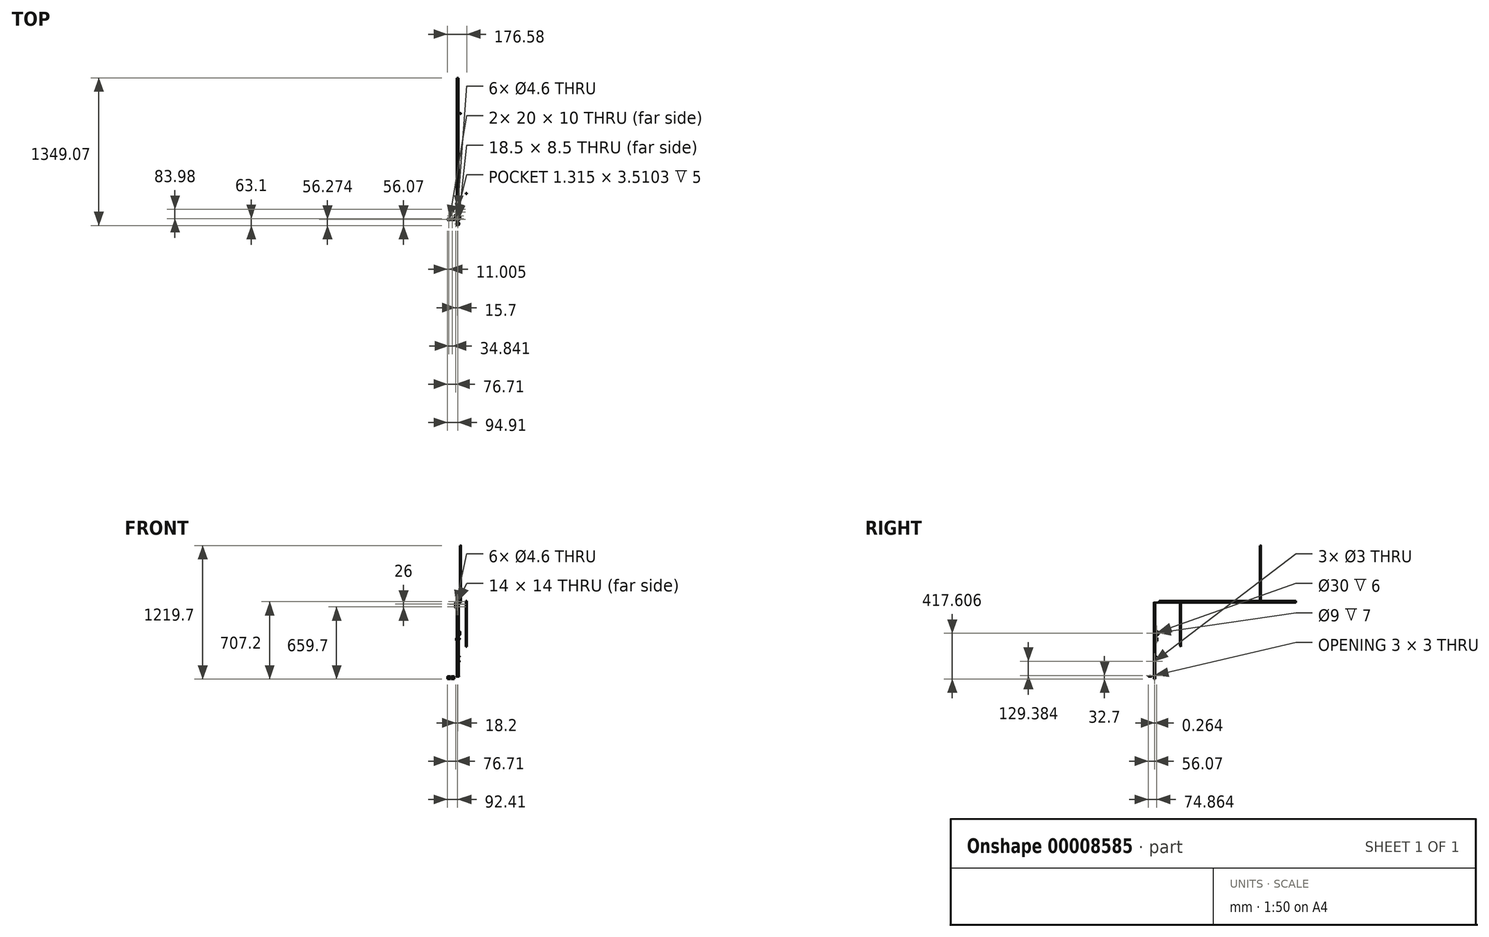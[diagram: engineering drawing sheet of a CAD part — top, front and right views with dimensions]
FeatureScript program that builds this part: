
annotation { "Feature Type Name" : "Feature", "Feature Type Description" : "" }
export const myFeature = defineFeature(function(context is Context, id is Id, definition is map)
    precondition{}
    {
        {
            var Q0;
            Q0=qCreatedBy(makeId("Front.planeOp"),FACE);
            var sketch = newSketch(context, id + "F0", { "sketchPlane" : qUnion([Q0])});
            skLineSegment(sketch, "E0.rect.bottom", {"start": v(-7.5, 7.5) * mm, "end": v(7.5, 7.5) * mm});
            skLineSegment(sketch, "E0.rect.top", {"start": v(-7.5, -7.5) * mm, "end": v(7.5, -7.5) * mm});
            skLineSegment(sketch, "E0.rect.left", {"start": v(-7.5, 7.5) * mm, "end": v(-7.5, -7.5) * mm});
            skLineSegment(sketch, "E0.rect.right", {"start": v(7.5, 7.5) * mm, "end": v(7.5, -7.5) * mm});
            skPoint(sketch, "E0.rect.middle", {"position": v(0, 0) * mm});
            skLineSegment(sketch, "E1.rect.bottom", {"start": v(-7, 7) * mm, "end": v(7, 7) * mm});
            skLineSegment(sketch, "E1.rect.top", {"start": v(-7, -7) * mm, "end": v(7, -7) * mm});
            skLineSegment(sketch, "E1.rect.left", {"start": v(-7, 7) * mm, "end": v(-7, -7) * mm});
            skLineSegment(sketch, "E1.rect.right", {"start": v(7, 7) * mm, "end": v(7, -7) * mm});
            skSolve(sketch);
        }
        {
            var Q0;
            Q0=qSketchRegion(id+"F0",true);
            extrude(context, id + "F1", {"entities" : qUnion([Q0]), "depth" : 950 * mm});
        }
        {
            var Q0;
            Q0=makeQuery(id+"F1.opExtrude","SWEPT_FACE",FACE,{"disambiguationData":[OSD([sQuery(id+"F0.wireOp",EDGE,"E0.rect.left")])]});
            var sketch = newSketch(context, id + "F2", { "sketchPlane" : qUnion([Q0])});
            skLineSegment(sketch, "E2.bottom", {"start": v(998.04, -7.5) * mm, "end": v(950, -7.5) * mm});
            skLineSegment(sketch, "E2.top", {"start": v(998, -9.5) * mm, "end": v(950, -9.5) * mm});
            skLineSegment(sketch, "E2.right", {"start": v(950, -7.5) * mm, "end": v(950, -9.5) * mm});
            skLineSegment(sketch, "E3.top", {"start": v(1000, -57.5) * mm, "end": v(998, -57.5) * mm});
            skLineSegment(sketch, "E3.left", {"start": v(1000, -9.5) * mm, "end": v(1000, -57.5) * mm});
            skLineSegment(sketch, "E3.right", {"start": v(998, -9.5) * mm, "end": v(998, -57.5) * mm});
            skArc(sketch, "E4", {"start": v(1000, -9.5) * mm, "mid": v(999.4, -8.07) * mm, "end": v(997.96, -7.5) * mm});
            skSolve(sketch);
        }
        {
            var Q0;
            Q0=qSketchRegion(id+"F2",true);
            extrude(context, id + "F3", {"entities" : qUnion([Q0]), "depth" : 16.4 * mm});
        }
        {
            var Q0;
            Q0=makeQuery(id+"F3.opExtrude","SWEPT_FACE",FACE,{"disambiguationData":[OSD([sQuery(id+"F2.wireOp",EDGE,"E3.left")])]});
            var sketch = newSketch(context, id + "F4", { "sketchPlane" : qUnion([Q0])});
            skCircle(sketch, "E5", {"center": v(-15.7, -21.5) * mm, "radius": 2.3 * mm});
            skCircle(sketch, "E6", {"center": v(-15.7, -45.5) * mm, "radius": 2.3 * mm});
            skSolve(sketch);
        }
        {
            var Q0;
            Q0=qSketchRegion(id+"F4",true);
            extrude(context, id + "F5", {"entities" : qUnion([Q0]), "operationType" : NewBodyOperationType.REMOVE, "oppositeDirection" : true, "depth" : 25 * mm});
        }
        {
            var Q0;
            Q0=makeQuery(id+"F3.opExtrude","SWEPT_FACE",FACE,{"disambiguationData":[OSD([sQuery(id+"F2.wireOp",EDGE,"E2.bottom")])]});
            var sketch = newSketch(context, id + "F6", { "sketchPlane" : qUnion([Q0])});
            skCircle(sketch, "E7", {"center": v(0, 12) * mm, "radius": 2.3 * mm});
            skCircle(sketch, "E8", {"center": v(0, -12) * mm, "radius": 2.3 * mm});
            skCircle(sketch, "E9", {"center": v(-15.7, -985.97) * mm, "radius": 2.3 * mm});
            skCircle(sketch, "E10", {"center": v(-15.7, -961.99) * mm, "radius": 2.3 * mm});
            skSolve(sketch);
        }
        {
            var Q0;
            Q0=makeQuery(id+"F6.imprint","IMPRINT",FACE,{"disambiguationData":[TD([[makeQuery(id+"F6.imprint","IMPRINT",EDGE,{"derivedFrom":sQuery(id+"F6.wireOp",EDGE,"E9")}),1.0]])]});
            var Q1;
            Q1=makeQuery(id+"F6.imprint","IMPRINT",FACE,{"disambiguationData":[TD([[makeQuery(id+"F6.imprint","IMPRINT",EDGE,{"derivedFrom":sQuery(id+"F6.wireOp",EDGE,"E10")}),1.0]])]});
            extrude(context, id + "F7", {"entities" : qUnion([Q0, Q1]), "operationType" : NewBodyOperationType.REMOVE, "oppositeDirection" : true, "depth" : 3 * mm});
        }
        {
            var Q0;
            Q0=makeQuery(id+"F3.opExtrude","SWEPT_FACE",FACE,{"disambiguationData":[OSD([sQuery(id+"F2.wireOp",EDGE,"E2.top")])]});
            var sketch = newSketch(context, id + "F8", { "sketchPlane" : qUnion([Q0])});
            skLineSegment(sketch, "E11.bottom", {"start": v(-7.5, 998) * mm, "end": v(12.5, 998) * mm});
            skLineSegment(sketch, "E11.top", {"start": v(-7.5, 988) * mm, "end": v(12.5, 988) * mm});
            skLineSegment(sketch, "E11.left", {"start": v(-7.5, 998) * mm, "end": v(-7.5, 988) * mm});
            skLineSegment(sketch, "E11.right", {"start": v(12.5, 998) * mm, "end": v(12.5, 988) * mm});
            skLineSegment(sketch, "E12.rect.bottom", {"start": v(-6.75, 988.75) * mm, "end": v(11.75, 988.75) * mm});
            skLineSegment(sketch, "E12.rect.top", {"start": v(-6.75, 997.25) * mm, "end": v(11.75, 997.25) * mm});
            skLineSegment(sketch, "E12.rect.left", {"start": v(-6.75, 988.75) * mm, "end": v(-6.75, 997.25) * mm});
            skLineSegment(sketch, "E12.rect.right", {"start": v(11.75, 988.75) * mm, "end": v(11.75, 997.25) * mm});
            skPoint(sketch, "E12.rect.middle", {"position": v(2.5, 993) * mm});
            skSolve(sketch);
        }
        {
            var Q0;
            Q0=makeQuery(id+"F8.imprint","IMPRINT",FACE,{"disambiguationData":[TD([[makeQuery(id+"F8.imprint","IMPRINT",EDGE,{"derivedFrom":sQuery(id+"F8.wireOp",EDGE,"E11.bottom")}),-1.0]])]});
            extrude(context, id + "F9", {"entities" : qUnion([Q0]), "depth" : 673 * mm});
        }
        {
            var Q0;
            Q0=makeQuery(id+"F9.opExtrude","SWEPT_FACE",FACE,{"disambiguationData":[OSD([sQuery(id+"F8.wireOp",EDGE,"E11.bottom")])]});
            var sketch = newSketch(context, id + "F10", { "sketchPlane" : qUnion([Q0])});
            skCircle(sketch, "E13", {"center": v(2.5, -23.5) * mm, "radius": 2.3 * mm});
            skCircle(sketch, "E14", {"center": v(2.5, -47.5) * mm, "radius": 2.3 * mm});
            skSolve(sketch);
        }
        {
            var Q0;
            Q0=qSketchRegion(id+"F10",true);
            extrude(context, id + "F11", {"entities" : qUnion([Q0]), "operationType" : NewBodyOperationType.REMOVE, "oppositeDirection" : true, "depth" : 11 * mm});
        }
        {
            var Q0;
            Q0=makeQuery(id+"F1.opExtrude","SWEPT_FACE",FACE,{"disambiguationData":[OSD([sQuery(id+"F0.wireOp",EDGE,"E0.rect.top")])]});
            var sketch = newSketch(context, id + "F12", { "sketchPlane" : qUnion([Q0])});
            skCircle(sketch, "E15", {"center": v(0, 901.99) * mm, "radius": 2.3 * mm});
            skCircle(sketch, "E16", {"center": v(0, 925.97) * mm, "radius": 2.3 * mm});
            skLineSegment(sketch, "E17", {"start": v(0, 950) * mm, "end": v(0, 925.97) * mm});
            skLineSegment(sketch, "E18", {"start": v(0, 925.97) * mm, "end": v(0, 901.99) * mm});
            skSolve(sketch);
        }
        {
            var Q0;
            Q0=makeQuery(id+"F12.imprint","IMPRINT",FACE,{"disambiguationData":[TD([[makeQuery(id+"F12.imprint","IMPRINT",EDGE,{"derivedFrom":sQuery(id+"F12.wireOp",EDGE,"E15")}),1.0]])]});
            var Q1;
            Q1=makeQuery(id+"F12.imprint","IMPRINT",FACE,{"disambiguationData":[TD([[makeQuery(id+"F12.imprint","IMPRINT",EDGE,{"derivedFrom":sQuery(id+"F12.wireOp",EDGE,"E16")}),1.0]])]});
            extrude(context, id + "F13", {"entities" : qUnion([Q0, Q1]), "operationType" : NewBodyOperationType.REMOVE, "oppositeDirection" : true, "depth" : 25 * mm});
        }
        {
            var Q0;
            Q0=makeQuery(id+"F9.opExtrude","CAP_FACE",FACE,{"disambiguationData":[OSD([sQuery(id+"F8.wireOp",EDGE,"E11.bottom"),sQuery(id+"F8.wireOp",EDGE,"E11.top"),sQuery(id+"F8.wireOp",EDGE,"E11.left"),sQuery(id+"F8.wireOp",EDGE,"E11.right"),sQuery(id+"F8.wireOp",EDGE,"E12.rect.bottom"),sQuery(id+"F8.wireOp",EDGE,"E12.rect.top"),sQuery(id+"F8.wireOp",EDGE,"E12.rect.left"),sQuery(id+"F8.wireOp",EDGE,"E12.rect.right")])],"isStart":false});
            var sketch = newSketch(context, id + "F14", { "sketchPlane" : qUnion([Q0])});
            skCircle(sketch, "E19", {"center": v(1.66, 1034.07) * mm, "radius": 15 * mm});
            skSolve(sketch);
        }
        {
            var Q0;
            Q0=qSketchRegion(id+"F14",true);
            extrude(context, id + "F15", {"entities" : qUnion([Q0]), "depth" : 2 * mm});
        }
        {
            var Q0;
            Q0=makeQuery(id+"F15.opExtrude","CAP_FACE",FACE,{"disambiguationData":[OSD([sQuery(id+"F14.wireOp",EDGE,"E19")])],"isStart":true});
            var sketch = newSketch(context, id + "F16", { "sketchPlane" : qUnion([Q0])});
            skLineSegment(sketch, "E20.rect.bottom", {"start": v(-7.59, -1038.32) * mm, "end": v(10.91, -1038.32) * mm});
            skLineSegment(sketch, "E20.rect.top", {"start": v(-7.59, -1029.82) * mm, "end": v(10.91, -1029.82) * mm});
            skLineSegment(sketch, "E20.rect.left", {"start": v(-7.59, -1038.32) * mm, "end": v(-7.59, -1029.82) * mm});
            skLineSegment(sketch, "E20.rect.right", {"start": v(10.91, -1038.32) * mm, "end": v(10.91, -1029.82) * mm});
            skPoint(sketch, "E20.rect.middle", {"position": v(1.66, -1034.07) * mm});
            skSolve(sketch);
        }
        {
            var Q0;
            Q0=qSketchRegion(id+"F16",true);
            extrude(context, id + "F17", {"entities" : qUnion([Q0]), "operationType" : NewBodyOperationType.ADD, "depth" : 3 * mm});
        }
        {
            var Q0;
            Q0=makeQuery(id+"F9.opExtrude","CAP_FACE",FACE,{"disambiguationData":[OSD([sQuery(id+"F8.wireOp",EDGE,"E11.bottom"),sQuery(id+"F8.wireOp",EDGE,"E11.top"),sQuery(id+"F8.wireOp",EDGE,"E11.left"),sQuery(id+"F8.wireOp",EDGE,"E11.right"),sQuery(id+"F8.wireOp",EDGE,"E12.rect.bottom"),sQuery(id+"F8.wireOp",EDGE,"E12.rect.top"),sQuery(id+"F8.wireOp",EDGE,"E12.rect.left"),sQuery(id+"F8.wireOp",EDGE,"E12.rect.right")])],"isStart":false});
            var sketch = newSketch(context, id + "F18", { "sketchPlane" : qUnion([Q0])});
            skLineSegment(sketch, "E21.rect.bottom", {"start": v(-56.56, 987.8) * mm, "end": v(-36.56, 987.8) * mm});
            skLineSegment(sketch, "E21.rect.top", {"start": v(-56.56, 997.8) * mm, "end": v(-36.56, 997.8) * mm});
            skLineSegment(sketch, "E21.rect.left", {"start": v(-56.56, 987.8) * mm, "end": v(-56.56, 997.8) * mm});
            skLineSegment(sketch, "E21.rect.right", {"start": v(-36.56, 987.8) * mm, "end": v(-36.56, 997.8) * mm});
            skPoint(sketch, "E21.rect.middle", {"position": v(-46.56, 992.8) * mm});
            skLineSegment(sketch, "E22.rect.bottom", {"start": v(-91.4, 987.8) * mm, "end": v(-71.4, 987.8) * mm});
            skLineSegment(sketch, "E22.rect.top", {"start": v(-91.4, 997.8) * mm, "end": v(-71.4, 997.8) * mm});
            skLineSegment(sketch, "E22.rect.left", {"start": v(-91.4, 987.8) * mm, "end": v(-91.4, 997.8) * mm});
            skLineSegment(sketch, "E22.rect.right", {"start": v(-71.4, 987.8) * mm, "end": v(-71.4, 997.8) * mm});
            skPoint(sketch, "E22.rect.middle", {"position": v(-81.4, 992.8) * mm});
            skLineSegment(sketch, "E23.rect.bottom", {"start": v(-92.4, 986.8) * mm, "end": v(-70.4, 986.8) * mm});
            skLineSegment(sketch, "E23.rect.top", {"start": v(-92.4, 998.8) * mm, "end": v(-70.4, 998.8) * mm});
            skLineSegment(sketch, "E23.rect.left", {"start": v(-92.4, 986.8) * mm, "end": v(-92.4, 998.8) * mm});
            skLineSegment(sketch, "E23.rect.right", {"start": v(-70.4, 986.8) * mm, "end": v(-70.4, 998.8) * mm});
            skLineSegment(sketch, "E24.rect.bottom", {"start": v(-57.56, 986.8) * mm, "end": v(-35.56, 986.8) * mm});
            skLineSegment(sketch, "E24.rect.top", {"start": v(-57.56, 998.8) * mm, "end": v(-35.56, 998.8) * mm});
            skLineSegment(sketch, "E24.rect.left", {"start": v(-57.56, 986.8) * mm, "end": v(-57.56, 998.8) * mm});
            skLineSegment(sketch, "E24.rect.right", {"start": v(-35.56, 986.8) * mm, "end": v(-35.56, 998.8) * mm});
            skSolve(sketch);
        }
        {
            var Q0;
            Q0=qSketchRegion(id+"F18",true);
            extrude(context, id + "F19", {"entities" : qUnion([Q0]), "depth" : 24.7 * mm});
        }
        {
            var Q0;
            Q0=makeQuery(id+"F19.opExtrude","SWEPT_FACE",FACE,{"disambiguationData":[OSD([sQuery(id+"F18.wireOp",EDGE,"E23.rect.bottom")])]});
            var sketch = newSketch(context, id + "F20", { "sketchPlane" : qUnion([Q0])});
            skLineSegment(sketch, "E25", {"start": v(81.4, -528.03) * mm, "end": v(87.58, -521.85) * mm});
            skLineSegment(sketch, "E26", {"start": v(87.58, -521.85) * mm, "end": v(81.4, -515.68) * mm});
            skLineSegment(sketch, "E27", {"start": v(81.4, -515.68) * mm, "end": v(75.23, -521.85) * mm});
            skLineSegment(sketch, "E28", {"start": v(75.23, -521.85) * mm, "end": v(81.4, -528.03) * mm});
            skSolve(sketch);
        }
        {
            var Q0;
            Q0=qSketchRegion(id+"F20",true);
            extrude(context, id + "F21", {"entities" : qUnion([Q0]), "operationType" : NewBodyOperationType.REMOVE, "oppositeDirection" : true, "depth" : 25 * mm});
        }
        {
            var Q0;
            Q0=makeQuery(id+"F19.opExtrude","CAP_FACE",FACE,{"disambiguationData":[OSD([sQuery(id+"F18.wireOp",EDGE,"E22.rect.bottom"),sQuery(id+"F18.wireOp",EDGE,"E22.rect.top"),sQuery(id+"F18.wireOp",EDGE,"E22.rect.left"),sQuery(id+"F18.wireOp",EDGE,"E22.rect.right"),sQuery(id+"F18.wireOp",EDGE,"E23.rect.bottom"),sQuery(id+"F18.wireOp",EDGE,"E23.rect.top"),sQuery(id+"F18.wireOp",EDGE,"E23.rect.left"),sQuery(id+"F18.wireOp",EDGE,"E23.rect.right")])],"isStart":false});
            var sketch = newSketch(context, id + "F22", { "sketchPlane" : qUnion([Q0])});
            skLineSegment(sketch, "E29", {"start": v(-70.4, 998.8) * mm, "end": v(-63.9, 998.8) * mm});
            skLineSegment(sketch, "E30", {"start": v(-63.9, 998.8) * mm, "end": v(-63.9, 997.8) * mm});
            skLineSegment(sketch, "E31", {"start": v(-63.9, 997.8) * mm, "end": v(-70.4, 997.8) * mm});
            skLineSegment(sketch, "E32", {"start": v(-70.4, 986.8) * mm, "end": v(-63.9, 986.8) * mm});
            skLineSegment(sketch, "E33", {"start": v(-63.9, 986.8) * mm, "end": v(-63.9, 987.8) * mm});
            skLineSegment(sketch, "E34", {"start": v(-63.9, 987.8) * mm, "end": v(-70.4, 987.8) * mm});
            skLineSegment(sketch, "E35", {"start": v(-35.56, 998.8) * mm, "end": v(-29.06, 998.8) * mm});
            skLineSegment(sketch, "E36", {"start": v(-29.06, 998.8) * mm, "end": v(-29.06, 997.8) * mm});
            skLineSegment(sketch, "E37", {"start": v(-29.06, 997.8) * mm, "end": v(-35.56, 997.8) * mm});
            skLineSegment(sketch, "E38", {"start": v(-35.56, 986.8) * mm, "end": v(-29.06, 986.8) * mm});
            skLineSegment(sketch, "E39", {"start": v(-29.06, 986.8) * mm, "end": v(-29.06, 987.8) * mm});
            skLineSegment(sketch, "E40", {"start": v(-29.06, 987.8) * mm, "end": v(-35.56, 987.8) * mm});
            skLineSegment(sketch, "E41", {"start": v(-70.4, 998.8) * mm, "end": v(-70.4, 997.8) * mm});
            skLineSegment(sketch, "E42", {"start": v(-70.4, 987.8) * mm, "end": v(-70.4, 986.8) * mm});
            skLineSegment(sketch, "E43", {"start": v(-35.56, 987.8) * mm, "end": v(-35.56, 986.8) * mm});
            skLineSegment(sketch, "E44", {"start": v(-35.56, 998.8) * mm, "end": v(-35.56, 997.8) * mm});
            skSolve(sketch);
        }
        {
            var Q0;
            Q0=qSketchRegion(id+"F22",true);
            extrude(context, id + "F23", {"entities" : qUnion([Q0]), "oppositeDirection" : true, "depth" : 24.7 * mm});
        }
        {
            var Q0;
            Q0=makeQuery(id+"F9.opExtrude","SWEPT_FACE",FACE,{"disambiguationData":[OSD([sQuery(id+"F8.wireOp",EDGE,"E11.right")])]});
            var sketch = newSketch(context, id + "F24", { "sketchPlane" : qUnion([Q0])});
            skCircle(sketch, "E45", {"center": v(-992.74, -545.12) * mm, "radius": 7.5 * mm});
            skSolve(sketch);
        }
        {
            var Q0;
            Q0=qSketchRegion(id+"F24",true);
            extrude(context, id + "F25", {"entities" : qUnion([Q0]), "depth" : 1.1 * mm});
        }
        {
            var Q0;
            Q0=makeQuery(id+"F25.opExtrude","CAP_FACE",FACE,{"disambiguationData":[OSD([sQuery(id+"F24.wireOp",EDGE,"E45")])],"isStart":false});
            var sketch = newSketch(context, id + "F26", { "sketchPlane" : qUnion([Q0])});
            skCircle(sketch, "E46", {"center": v(-992.74, -545.12) * mm, "radius": 5.25 * mm});
            skSolve(sketch);
        }
        {
            var Q0;
            Q0=qSketchRegion(id+"F26",true);
            extrude(context, id + "F27", {"entities" : qUnion([Q0]), "operationType" : NewBodyOperationType.ADD, "depth" : 5.5 * mm});
        }
        {
            var Q0;
            Q0=makeQuery(id+"F27.opExtrude","CAP_FACE",FACE,{"disambiguationData":[OSD([sQuery(id+"F26.wireOp",EDGE,"E46")])],"isStart":false});
            var sketch = newSketch(context, id + "F28", { "sketchPlane" : qUnion([Q0])});
            skSolve(sketch);
        }
        {
            var Q0;
            Q0=makeQuery(id+"F28.imprint","IMPRINT",FACE,{"disambiguationData":[TD([[makeQuery(id+"F28.imprint","IMPRINT",EDGE,{"derivedFrom":makeQuery(id+"F27.opExtrude","CAP_EDGE",EDGE,{"disambiguationData":[OSD([sQuery(id+"F26.wireOp",EDGE,"E46")])],"isStart":false})}),1.0]])]});
            var sketch = newSketch(context, id + "F29", { "sketchPlane" : qUnion([Q0])});
            skCircle(sketch, "E47.0", {"center": v(-992.74, -545.12) * mm, "radius": 5.25 * mm});
            skLineSegment(sketch, "E48", {"start": v(-993.24, -539.89) * mm, "end": v(-992.32, -539.88) * mm});
            skLineSegment(sketch, "E49", {"start": v(-992.32, -539.88) * mm, "end": v(-992.53, -539.3) * mm});
            skLineSegment(sketch, "E50", {"start": v(-992.53, -539.3) * mm, "end": v(-993.01, -539.3) * mm});
            skLineSegment(sketch, "E51", {"start": v(-993.01, -539.3) * mm, "end": v(-993.24, -539.89) * mm});
            skSolve(sketch);
        }
        {
            var Q0;
            {var subQ1=sQuery(id+"F29.wireOp",EDGE,"E49");Q0=makeQuery(id+"F29.imprint","IMPRINT",FACE,{"disambiguationData":[TD([[makeQuery(id+"F29.imprint","IMPRINT",EDGE,{"derivedFrom":subQ1}),1.0]])]});}
            extrude(context, id + "F30", {"entities" : qUnion([Q0]), "oppositeDirection" : true, "depth" : 5.5 * mm});
        }
        {
            var Q0;
            Q0=makeQuery(id+"F30.opExtrude","SWEPT_BODY",BODY,{"disambiguationData":[OSD([sQuery(id+"F29.wireOp",EDGE,"E47.0"),sQuery(id+"F29.wireOp",EDGE,"E49"),sQuery(id+"F29.wireOp",EDGE,"E50"),sQuery(id+"F29.wireOp",EDGE,"E51")])]});
            var Q1;
            Q1=makeQuery(id+"F27.opExtrude","CAP_EDGE",EDGE,{"disambiguationData":[OSD([sQuery(id+"F26.wireOp",EDGE,"E46")])],"isStart":false});
            circularPattern(context, id + "F31", {"entities" : qUnion([Q0]), "axis" : qUnion([Q1]), "angle" : 10 * degree, "instanceCount" : round(40), "computeTransformsWithoutBuiltin" : true});
        }
        {
            var Q0;
            Q0=makeQuery(id+"F25.opExtrude","CAP_FACE",FACE,{"disambiguationData":[OSD([sQuery(id+"F24.wireOp",EDGE,"E45")])],"isStart":true});
            var sketch = newSketch(context, id + "F32", { "sketchPlane" : qUnion([Q0])});
            skCircle(sketch, "E52", {"center": v(992.74, -545.12) * mm, "radius": 1.5 * mm});
            skSolve(sketch);
        }
        {
            var Q0;
            Q0=qSketchRegion(id+"F32",true);
            extrude(context, id + "F33", {"entities" : qUnion([Q0]), "operationType" : NewBodyOperationType.REMOVE, "oppositeDirection" : true, "depth" : 25 * mm});
        }
        {
            var Q0;
            Q0=makeQuery(id+"F9.opExtrude","SWEPT_FACE",FACE,{"disambiguationData":[OSD([sQuery(id+"F8.wireOp",EDGE,"E11.right")])]});
            var sketch = newSketch(context, id + "F34", { "sketchPlane" : qUnion([Q0])});
            skLineSegment(sketch, "E53.bottom", {"start": v(-980.2, -333.62) * mm, "end": v(-968.2, -333.62) * mm});
            skLineSegment(sketch, "E53.top", {"start": v(-980.2, -356.12) * mm, "end": v(-968.2, -356.12) * mm});
            skLineSegment(sketch, "E53.left", {"start": v(-980.2, -333.62) * mm, "end": v(-980.2, -356.12) * mm});
            skLineSegment(sketch, "E53.right", {"start": v(-968.2, -333.62) * mm, "end": v(-968.2, -356.12) * mm});
            skSolve(sketch);
        }
        {
            var Q0;
            Q0=qSketchRegion(id+"F34",true);
            extrude(context, id + "F35", {"entities" : qUnion([Q0]), "oppositeDirection" : true, "depth" : 26.5 * mm});
        }
        {
            var Q0;
            Q0=makeQuery(id+"F35.opExtrude","SWEPT_FACE",FACE,{"disambiguationData":[OSD([sQuery(id+"F34.wireOp",EDGE,"E53.right")])]});
            var sketch = newSketch(context, id + "F36", { "sketchPlane" : qUnion([Q0])});
            skLineSegment(sketch, "E54.bottom", {"start": v(-7, -356.12) * mm, "end": v(-8.5, -356.12) * mm});
            skLineSegment(sketch, "E54.top", {"start": v(-7, -361.12) * mm, "end": v(-8.5, -361.12) * mm});
            skLineSegment(sketch, "E54.left", {"start": v(-7, -356.12) * mm, "end": v(-7, -361.12) * mm});
            skLineSegment(sketch, "E54.right", {"start": v(-8.5, -356.12) * mm, "end": v(-8.5, -361.12) * mm});
            skLineSegment(sketch, "E55.bottom", {"start": v(-7, -333.62) * mm, "end": v(-8.5, -333.62) * mm});
            skLineSegment(sketch, "E55.top", {"start": v(-7, -328.62) * mm, "end": v(-8.5, -328.62) * mm});
            skLineSegment(sketch, "E55.left", {"start": v(-7, -333.62) * mm, "end": v(-7, -328.62) * mm});
            skLineSegment(sketch, "E55.right", {"start": v(-8.5, -333.62) * mm, "end": v(-8.5, -328.62) * mm});
            skSolve(sketch);
        }
        {
            var Q0;
            Q0=qSketchRegion(id+"F36",true);
            extrude(context, id + "F37", {"entities" : qUnion([Q0]), "oppositeDirection" : true, "depth" : 12 * mm});
        }
        {
            var Q0;
            Q0=makeQuery(id+"F35.opExtrude","CAP_FACE",FACE,{"disambiguationData":[OSD([sQuery(id+"F34.wireOp",EDGE,"E53.bottom"),sQuery(id+"F34.wireOp",EDGE,"E53.top"),sQuery(id+"F34.wireOp",EDGE,"E53.left"),sQuery(id+"F34.wireOp",EDGE,"E53.right")])],"isStart":true});
            var sketch = newSketch(context, id + "F38", { "sketchPlane" : qUnion([Q0])});
            skLineSegment(sketch, "E56", {"start": v(-974.2, -333.62) * mm, "end": v(-974.2, -356.12) * mm});
            skCircle(sketch, "E57", {"center": v(-974.2, -339.6) * mm, "radius": 5.72 * mm});
            skSolve(sketch);
        }
        {
            var Q0;
            Q0=qSketchRegion(id+"F38",true);
            extrude(context, id + "F39", {"entities" : qUnion([Q0]), "operationType" : NewBodyOperationType.ADD, "depth" : 4.5 * mm});
        }
        {
            var Q0;
            Q0=makeQuery(id+"F39.opExtrude","CAP_FACE",FACE,{"disambiguationData":[OSD([sQuery(id+"F38.wireOp",EDGE,"E57")])],"isStart":false});
            var sketch = newSketch(context, id + "F40", { "sketchPlane" : qUnion([Q0])});
            skCircle(sketch, "E58", {"center": v(-974.2, -339.6) * mm, "radius": 2 * mm});
            skSolve(sketch);
        }
        {
            var Q0;
            Q0=qSketchRegion(id+"F40",true);
            extrude(context, id + "F41", {"entities" : qUnion([Q0]), "operationType" : NewBodyOperationType.ADD, "depth" : 4.5 * mm});
        }
        {
            var Q0;
            Q0=makeQuery(id+"F41.opExtrude","CAP_FACE",FACE,{"disambiguationData":[OSD([sQuery(id+"F40.wireOp",EDGE,"E58")])],"isStart":false});
            var sketch = newSketch(context, id + "F42", { "sketchPlane" : qUnion([Q0])});
            skLineSegment(sketch, "E59", {"start": v(-973.99, -341.58) * mm, "end": v(-974.14, -341.98) * mm});
            skLineSegment(sketch, "E60", {"start": v(-974.14, -341.98) * mm, "end": v(-974.35, -341.98) * mm});
            skLineSegment(sketch, "E61", {"start": v(-974.35, -341.98) * mm, "end": v(-974.5, -341.57) * mm});
            skLineSegment(sketch, "E62", {"start": v(-974.5, -341.57) * mm, "end": v(-973.99, -341.58) * mm});
            skSolve(sketch);
        }
        {
            var Q0;
            Q0=qSketchRegion(id+"F42",true);
            extrude(context, id + "F43", {"entities" : qUnion([Q0]), "oppositeDirection" : true, "depth" : 4.5 * mm});
        }
        {
            var Q0;
            Q0=makeQuery(id+"F43.opExtrude","SWEPT_BODY",BODY,{"disambiguationData":[OSD([sQuery(id+"F42.wireOp",EDGE,"E59"),sQuery(id+"F42.wireOp",EDGE,"E60"),sQuery(id+"F42.wireOp",EDGE,"E61"),sQuery(id+"F42.wireOp",EDGE,"E62")])]});
            var Q1;
            Q1=makeQuery(id+"F41.opExtrude","CAP_EDGE",EDGE,{"disambiguationData":[OSD([sQuery(id+"F40.wireOp",EDGE,"E58")])],"isStart":false});
            circularPattern(context, id + "F44", {"entities" : qUnion([Q0]), "axis" : qUnion([Q1]), "angle" : 20 * degree, "instanceCount" : round(30), "computeTransformsWithoutBuiltin" : true});
        }
        {
            var Q0;
            Q0=makeQuery(id+"F35.opExtrude","SWEPT_BODY",BODY,{"disambiguationData":[OSD([sQuery(id+"F34.wireOp",EDGE,"E53.bottom"),sQuery(id+"F34.wireOp",EDGE,"E53.top"),sQuery(id+"F34.wireOp",EDGE,"E53.left"),sQuery(id+"F34.wireOp",EDGE,"E53.right")])]});
            var Q1;
            Q1=makeQuery(id+"F37.opExtrude","SWEPT_BODY",BODY,{"disambiguationData":[OSD([sQuery(id+"F36.wireOp",EDGE,"E54.bottom"),sQuery(id+"F36.wireOp",EDGE,"E54.top"),sQuery(id+"F36.wireOp",EDGE,"E54.left"),sQuery(id+"F36.wireOp",EDGE,"E54.right")])]});
            var Q2;
            Q2=makeQuery(id+"F37.opExtrude","SWEPT_BODY",BODY,{"disambiguationData":[OSD([sQuery(id+"F36.wireOp",EDGE,"E55.bottom"),sQuery(id+"F36.wireOp",EDGE,"E55.top"),sQuery(id+"F36.wireOp",EDGE,"E55.left"),sQuery(id+"F36.wireOp",EDGE,"E55.right")])]});
            var Q3;
            Q3=makeQuery(id+"F44.opPattern","COPY",BODY,{"derivedFrom":makeQuery(id+"F43.opExtrude","SWEPT_BODY",BODY,{"disambiguationData":[OSD([sQuery(id+"F42.wireOp",EDGE,"E59"),sQuery(id+"F42.wireOp",EDGE,"E60"),sQuery(id+"F42.wireOp",EDGE,"E61"),sQuery(id+"F42.wireOp",EDGE,"E62")])]}),"instanceName":"14"});
            var Q4;
            Q4=makeQuery(id+"F44.opPattern","COPY",BODY,{"derivedFrom":makeQuery(id+"F43.opExtrude","SWEPT_BODY",BODY,{"disambiguationData":[OSD([sQuery(id+"F42.wireOp",EDGE,"E59"),sQuery(id+"F42.wireOp",EDGE,"E60"),sQuery(id+"F42.wireOp",EDGE,"E61"),sQuery(id+"F42.wireOp",EDGE,"E62")])]}),"instanceName":"12"});
            var Q5;
            Q5=makeQuery(id+"F44.opPattern","COPY",BODY,{"derivedFrom":makeQuery(id+"F43.opExtrude","SWEPT_BODY",BODY,{"disambiguationData":[OSD([sQuery(id+"F42.wireOp",EDGE,"E59"),sQuery(id+"F42.wireOp",EDGE,"E60"),sQuery(id+"F42.wireOp",EDGE,"E61"),sQuery(id+"F42.wireOp",EDGE,"E62")])]}),"instanceName":"13"});
            var Q6;
            Q6=makeQuery(id+"F44.opPattern","COPY",BODY,{"derivedFrom":makeQuery(id+"F43.opExtrude","SWEPT_BODY",BODY,{"disambiguationData":[OSD([sQuery(id+"F42.wireOp",EDGE,"E59"),sQuery(id+"F42.wireOp",EDGE,"E60"),sQuery(id+"F42.wireOp",EDGE,"E61"),sQuery(id+"F42.wireOp",EDGE,"E62")])]}),"instanceName":"17"});
            var Q7;
            Q7=makeQuery(id+"F44.opPattern","COPY",BODY,{"derivedFrom":makeQuery(id+"F43.opExtrude","SWEPT_BODY",BODY,{"disambiguationData":[OSD([sQuery(id+"F42.wireOp",EDGE,"E59"),sQuery(id+"F42.wireOp",EDGE,"E60"),sQuery(id+"F42.wireOp",EDGE,"E61"),sQuery(id+"F42.wireOp",EDGE,"E62")])]}),"instanceName":"15"});
            var Q8;
            Q8=makeQuery(id+"F44.opPattern","COPY",BODY,{"derivedFrom":makeQuery(id+"F43.opExtrude","SWEPT_BODY",BODY,{"disambiguationData":[OSD([sQuery(id+"F42.wireOp",EDGE,"E59"),sQuery(id+"F42.wireOp",EDGE,"E60"),sQuery(id+"F42.wireOp",EDGE,"E61"),sQuery(id+"F42.wireOp",EDGE,"E62")])]}),"instanceName":"11"});
            var Q9;
            Q9=makeQuery(id+"F44.opPattern","COPY",BODY,{"derivedFrom":makeQuery(id+"F43.opExtrude","SWEPT_BODY",BODY,{"disambiguationData":[OSD([sQuery(id+"F42.wireOp",EDGE,"E59"),sQuery(id+"F42.wireOp",EDGE,"E60"),sQuery(id+"F42.wireOp",EDGE,"E61"),sQuery(id+"F42.wireOp",EDGE,"E62")])]}),"instanceName":"16"});
            var Q10;
            Q10=makeQuery(id+"F44.opPattern","COPY",BODY,{"derivedFrom":makeQuery(id+"F43.opExtrude","SWEPT_BODY",BODY,{"disambiguationData":[OSD([sQuery(id+"F42.wireOp",EDGE,"E59"),sQuery(id+"F42.wireOp",EDGE,"E60"),sQuery(id+"F42.wireOp",EDGE,"E61"),sQuery(id+"F42.wireOp",EDGE,"E62")])]}),"instanceName":"5"});
            var Q11;
            Q11=makeQuery(id+"F43.opExtrude","SWEPT_BODY",BODY,{"disambiguationData":[OSD([sQuery(id+"F42.wireOp",EDGE,"E59"),sQuery(id+"F42.wireOp",EDGE,"E60"),sQuery(id+"F42.wireOp",EDGE,"E61"),sQuery(id+"F42.wireOp",EDGE,"E62")])]});
            var Q12;
            Q12=makeQuery(id+"F44.opPattern","COPY",BODY,{"derivedFrom":makeQuery(id+"F43.opExtrude","SWEPT_BODY",BODY,{"disambiguationData":[OSD([sQuery(id+"F42.wireOp",EDGE,"E59"),sQuery(id+"F42.wireOp",EDGE,"E60"),sQuery(id+"F42.wireOp",EDGE,"E61"),sQuery(id+"F42.wireOp",EDGE,"E62")])]}),"instanceName":"23"});
            var Q13;
            Q13=makeQuery(id+"F44.opPattern","COPY",BODY,{"derivedFrom":makeQuery(id+"F43.opExtrude","SWEPT_BODY",BODY,{"disambiguationData":[OSD([sQuery(id+"F42.wireOp",EDGE,"E59"),sQuery(id+"F42.wireOp",EDGE,"E60"),sQuery(id+"F42.wireOp",EDGE,"E61"),sQuery(id+"F42.wireOp",EDGE,"E62")])]}),"instanceName":"29"});
            var Q14;
            Q14=makeQuery(id+"F44.opPattern","COPY",BODY,{"derivedFrom":makeQuery(id+"F43.opExtrude","SWEPT_BODY",BODY,{"disambiguationData":[OSD([sQuery(id+"F42.wireOp",EDGE,"E59"),sQuery(id+"F42.wireOp",EDGE,"E60"),sQuery(id+"F42.wireOp",EDGE,"E61"),sQuery(id+"F42.wireOp",EDGE,"E62")])]}),"instanceName":"7"});
            var Q15;
            Q15=makeQuery(id+"F44.opPattern","COPY",BODY,{"derivedFrom":makeQuery(id+"F43.opExtrude","SWEPT_BODY",BODY,{"disambiguationData":[OSD([sQuery(id+"F42.wireOp",EDGE,"E59"),sQuery(id+"F42.wireOp",EDGE,"E60"),sQuery(id+"F42.wireOp",EDGE,"E61"),sQuery(id+"F42.wireOp",EDGE,"E62")])]}),"instanceName":"4"});
            var Q16;
            Q16=makeQuery(id+"F44.opPattern","COPY",BODY,{"derivedFrom":makeQuery(id+"F43.opExtrude","SWEPT_BODY",BODY,{"disambiguationData":[OSD([sQuery(id+"F42.wireOp",EDGE,"E59"),sQuery(id+"F42.wireOp",EDGE,"E60"),sQuery(id+"F42.wireOp",EDGE,"E61"),sQuery(id+"F42.wireOp",EDGE,"E62")])]}),"instanceName":"28"});
            var Q17;
            Q17=makeQuery(id+"F44.opPattern","COPY",BODY,{"derivedFrom":makeQuery(id+"F43.opExtrude","SWEPT_BODY",BODY,{"disambiguationData":[OSD([sQuery(id+"F42.wireOp",EDGE,"E59"),sQuery(id+"F42.wireOp",EDGE,"E60"),sQuery(id+"F42.wireOp",EDGE,"E61"),sQuery(id+"F42.wireOp",EDGE,"E62")])]}),"instanceName":"2"});
            var Q18;
            Q18=makeQuery(id+"F44.opPattern","COPY",BODY,{"derivedFrom":makeQuery(id+"F43.opExtrude","SWEPT_BODY",BODY,{"disambiguationData":[OSD([sQuery(id+"F42.wireOp",EDGE,"E59"),sQuery(id+"F42.wireOp",EDGE,"E60"),sQuery(id+"F42.wireOp",EDGE,"E61"),sQuery(id+"F42.wireOp",EDGE,"E62")])]}),"instanceName":"1"});
            var Q19;
            Q19=makeQuery(id+"F44.opPattern","COPY",BODY,{"derivedFrom":makeQuery(id+"F43.opExtrude","SWEPT_BODY",BODY,{"disambiguationData":[OSD([sQuery(id+"F42.wireOp",EDGE,"E59"),sQuery(id+"F42.wireOp",EDGE,"E60"),sQuery(id+"F42.wireOp",EDGE,"E61"),sQuery(id+"F42.wireOp",EDGE,"E62")])]}),"instanceName":"10"});
            var Q20;
            Q20=makeQuery(id+"F44.opPattern","COPY",BODY,{"derivedFrom":makeQuery(id+"F43.opExtrude","SWEPT_BODY",BODY,{"disambiguationData":[OSD([sQuery(id+"F42.wireOp",EDGE,"E59"),sQuery(id+"F42.wireOp",EDGE,"E60"),sQuery(id+"F42.wireOp",EDGE,"E61"),sQuery(id+"F42.wireOp",EDGE,"E62")])]}),"instanceName":"20"});
            var Q21;
            Q21=makeQuery(id+"F44.opPattern","COPY",BODY,{"derivedFrom":makeQuery(id+"F43.opExtrude","SWEPT_BODY",BODY,{"disambiguationData":[OSD([sQuery(id+"F42.wireOp",EDGE,"E59"),sQuery(id+"F42.wireOp",EDGE,"E60"),sQuery(id+"F42.wireOp",EDGE,"E61"),sQuery(id+"F42.wireOp",EDGE,"E62")])]}),"instanceName":"3"});
            var Q22;
            Q22=makeQuery(id+"F44.opPattern","COPY",BODY,{"derivedFrom":makeQuery(id+"F43.opExtrude","SWEPT_BODY",BODY,{"disambiguationData":[OSD([sQuery(id+"F42.wireOp",EDGE,"E59"),sQuery(id+"F42.wireOp",EDGE,"E60"),sQuery(id+"F42.wireOp",EDGE,"E61"),sQuery(id+"F42.wireOp",EDGE,"E62")])]}),"instanceName":"27"});
            var Q23;
            Q23=makeQuery(id+"F44.opPattern","COPY",BODY,{"derivedFrom":makeQuery(id+"F43.opExtrude","SWEPT_BODY",BODY,{"disambiguationData":[OSD([sQuery(id+"F42.wireOp",EDGE,"E59"),sQuery(id+"F42.wireOp",EDGE,"E60"),sQuery(id+"F42.wireOp",EDGE,"E61"),sQuery(id+"F42.wireOp",EDGE,"E62")])]}),"instanceName":"6"});
            var Q24;
            Q24=makeQuery(id+"F44.opPattern","COPY",BODY,{"derivedFrom":makeQuery(id+"F43.opExtrude","SWEPT_BODY",BODY,{"disambiguationData":[OSD([sQuery(id+"F42.wireOp",EDGE,"E59"),sQuery(id+"F42.wireOp",EDGE,"E60"),sQuery(id+"F42.wireOp",EDGE,"E61"),sQuery(id+"F42.wireOp",EDGE,"E62")])]}),"instanceName":"8"});
            var Q25;
            Q25=makeQuery(id+"F44.opPattern","COPY",BODY,{"derivedFrom":makeQuery(id+"F43.opExtrude","SWEPT_BODY",BODY,{"disambiguationData":[OSD([sQuery(id+"F42.wireOp",EDGE,"E59"),sQuery(id+"F42.wireOp",EDGE,"E60"),sQuery(id+"F42.wireOp",EDGE,"E61"),sQuery(id+"F42.wireOp",EDGE,"E62")])]}),"instanceName":"18"});
            var Q26;
            Q26=makeQuery(id+"F44.opPattern","COPY",BODY,{"derivedFrom":makeQuery(id+"F43.opExtrude","SWEPT_BODY",BODY,{"disambiguationData":[OSD([sQuery(id+"F42.wireOp",EDGE,"E59"),sQuery(id+"F42.wireOp",EDGE,"E60"),sQuery(id+"F42.wireOp",EDGE,"E61"),sQuery(id+"F42.wireOp",EDGE,"E62")])]}),"instanceName":"25"});
            var Q27;
            Q27=makeQuery(id+"F44.opPattern","COPY",BODY,{"derivedFrom":makeQuery(id+"F43.opExtrude","SWEPT_BODY",BODY,{"disambiguationData":[OSD([sQuery(id+"F42.wireOp",EDGE,"E59"),sQuery(id+"F42.wireOp",EDGE,"E60"),sQuery(id+"F42.wireOp",EDGE,"E61"),sQuery(id+"F42.wireOp",EDGE,"E62")])]}),"instanceName":"19"});
            var Q28;
            Q28=makeQuery(id+"F44.opPattern","COPY",BODY,{"derivedFrom":makeQuery(id+"F43.opExtrude","SWEPT_BODY",BODY,{"disambiguationData":[OSD([sQuery(id+"F42.wireOp",EDGE,"E59"),sQuery(id+"F42.wireOp",EDGE,"E60"),sQuery(id+"F42.wireOp",EDGE,"E61"),sQuery(id+"F42.wireOp",EDGE,"E62")])]}),"instanceName":"22"});
            var Q29;
            Q29=makeQuery(id+"F44.opPattern","COPY",BODY,{"derivedFrom":makeQuery(id+"F43.opExtrude","SWEPT_BODY",BODY,{"disambiguationData":[OSD([sQuery(id+"F42.wireOp",EDGE,"E59"),sQuery(id+"F42.wireOp",EDGE,"E60"),sQuery(id+"F42.wireOp",EDGE,"E61"),sQuery(id+"F42.wireOp",EDGE,"E62")])]}),"instanceName":"21"});
            var Q30;
            Q30=makeQuery(id+"F44.opPattern","COPY",BODY,{"derivedFrom":makeQuery(id+"F43.opExtrude","SWEPT_BODY",BODY,{"disambiguationData":[OSD([sQuery(id+"F42.wireOp",EDGE,"E59"),sQuery(id+"F42.wireOp",EDGE,"E60"),sQuery(id+"F42.wireOp",EDGE,"E61"),sQuery(id+"F42.wireOp",EDGE,"E62")])]}),"instanceName":"9"});
            var Q31;
            Q31=makeQuery(id+"F44.opPattern","COPY",BODY,{"derivedFrom":makeQuery(id+"F43.opExtrude","SWEPT_BODY",BODY,{"disambiguationData":[OSD([sQuery(id+"F42.wireOp",EDGE,"E59"),sQuery(id+"F42.wireOp",EDGE,"E60"),sQuery(id+"F42.wireOp",EDGE,"E61"),sQuery(id+"F42.wireOp",EDGE,"E62")])]}),"instanceName":"24"});
            var Q32;
            Q32=makeQuery(id+"F44.opPattern","COPY",BODY,{"derivedFrom":makeQuery(id+"F43.opExtrude","SWEPT_BODY",BODY,{"disambiguationData":[OSD([sQuery(id+"F42.wireOp",EDGE,"E59"),sQuery(id+"F42.wireOp",EDGE,"E60"),sQuery(id+"F42.wireOp",EDGE,"E61"),sQuery(id+"F42.wireOp",EDGE,"E62")])]}),"instanceName":"26"});
            booleanBodies(context, id + "F45", {"operationType" : BooleanOperationType.UNION, "tools" : qUnion([Q0, Q1, Q2, Q3, Q4, Q5, Q6, Q7, Q8, Q9, Q10, Q11, Q12, Q13, Q14, Q15, Q16, Q17, Q18, Q19, Q20, Q21, Q22, Q23, Q24, Q25, Q26, Q27, Q28, Q29, Q30, Q31, Q32])});
        }
        {
            var Q0;
            Q0=makeQuery(id+"F37.opExtrude","SWEPT_FACE",FACE,{"disambiguationData":[OSD([sQuery(id+"F36.wireOp",EDGE,"E54.right")])]});
            var sketch = newSketch(context, id + "F46", { "sketchPlane" : qUnion([Q0])});
            skArc(sketch, "E63", {"start": v(-973.78, -360.4) * mm, "mid": v(-974.2, -358.7) * mm, "end": v(-974.63, -360.4) * mm});
            skLineSegment(sketch, "E64.rect.bottom", {"start": v(-974.63, -361.99) * mm, "end": v(-973.78, -361.99) * mm});
            skLineSegment(sketch, "E64.rect.left", {"start": v(-974.63, -361.99) * mm, "end": v(-974.63, -360.4) * mm});
            skLineSegment(sketch, "E64.rect.right", {"start": v(-973.78, -361.99) * mm, "end": v(-973.78, -360.4) * mm});
            skPoint(sketch, "E64.rect.middle", {"position": v(-974.2, -361.12) * mm});
            skPoint(sketch, "E65.trimOffspring.end.orphan", {"position": v(-974.2, -356.12) * mm});
            skSolve(sketch);
        }
        {
            var Q0;
            {var subQ5=sQuery(id+"F46.wireOp",EDGE,"E63");Q0=makeQuery(id+"F46.imprint","IMPRINT",FACE,{"disambiguationData":[TD([[makeQuery(id+"F46.imprint","IMPRINT",EDGE,{"derivedFrom":subQ5}),1.0]])]});}
            extrude(context, id + "F47", {"entities" : qUnion([Q0]), "operationType" : NewBodyOperationType.REMOVE, "oppositeDirection" : true, "depth" : 25 * mm});
        }
        {
            var Q0;
            Q0=makeQuery(id+"F37.opExtrude","SWEPT_FACE",FACE,{"disambiguationData":[OSD([sQuery(id+"F36.wireOp",EDGE,"E55.right")])]});
            var sketch = newSketch(context, id + "F48", { "sketchPlane" : qUnion([Q0])});
            skArc(sketch, "E66", {"start": v(0.42, -0.22) * mm, "mid": v(0, 1.48) * mm, "end": v(-0.42, -0.22) * mm});
            skLineSegment(sketch, "E67.rect.bottom", {"start": v(-0.42, -1.81) * mm, "end": v(0.42, -1.81) * mm});
            skLineSegment(sketch, "E67.rect.left", {"start": v(-0.42, -1.81) * mm, "end": v(-0.42, -0.22) * mm});
            skLineSegment(sketch, "E67.rect.right", {"start": v(0.42, -1.81) * mm, "end": v(0.42, -0.22) * mm});
            skPoint(sketch, "E67.rect.middle", {"position": v(0, -0.95) * mm});
            skPoint(sketch, "E68.trimOffspring.end.orphan", {"position": v(0, 4.05) * mm});
            skLineSegment(sketch, "E69.0.4", {"start": v(-980.2, -356.12) * mm, "end": v(-980.2, -361.12) * mm});
            skLineSegment(sketch, "E70.0.MirrorCS", {"start": v(-974.63, -328.62) * mm, "end": v(-974.63, -329.35) * mm});
            skLineSegment(sketch, "E71.0.MirrorCS", {"start": v(-973.78, -329.35) * mm, "end": v(-973.78, -328.62) * mm});
            skArc(sketch, "E72.0.MirrorCS", {"start": v(-974.63, -329.35) * mm, "mid": v(-974.2, -331.06) * mm, "end": v(-973.78, -329.35) * mm});
            skLineSegment(sketch, "E73", {"start": v(-973.78, -328.62) * mm, "end": v(-974.63, -328.62) * mm});
            skSolve(sketch);
        }
        {
            var Q0;
            Q0=makeQuery(id+"F48.imprint","IMPRINT",FACE,{"disambiguationData":[TD([[makeQuery(id+"F48.imprint","IMPRINT",EDGE,{"derivedFrom":sQuery(id+"F48.wireOp",EDGE,"E70.0.MirrorCS")}),1.0]])]});
            extrude(context, id + "F49", {"entities" : qUnion([Q0]), "operationType" : NewBodyOperationType.REMOVE, "oppositeDirection" : true, "depth" : 25 * mm});
        }
        {
            var Q0;
            Q0=makeQuery(id+"F35.opExtrude","CAP_FACE",FACE,{"disambiguationData":[OSD([sQuery(id+"F34.wireOp",EDGE,"E53.bottom"),sQuery(id+"F34.wireOp",EDGE,"E53.top"),sQuery(id+"F34.wireOp",EDGE,"E53.left"),sQuery(id+"F34.wireOp",EDGE,"E53.right")])],"isStart":true});
            var sketch = newSketch(context, id + "F50", { "sketchPlane" : qUnion([Q0])});
            skArc(sketch, "E74", {"start": v(-975.76, -345.1) * mm, "mid": v(-974.2, -348.9) * mm, "end": v(-972.65, -345.1) * mm});
            skArc(sketch, "E75.0", {"start": v(-975.76, -345.1) * mm, "mid": v(-974.2, -345.32) * mm, "end": v(-972.65, -345.1) * mm});
            skPoint(sketch, "E76.start.orphan", {"position": v(-974.2, -356.12) * mm});
            skSolve(sketch);
        }
        {
            var Q0;
            Q0=makeQuery(id+"F50.imprint","IMPRINT",FACE,{"disambiguationData":[TD([[makeQuery(id+"F50.imprint","IMPRINT",EDGE,{"derivedFrom":sQuery(id+"F50.wireOp",EDGE,"E74")}),1.0]])]});
            extrude(context, id + "F51", {"entities" : qUnion([Q0]), "operationType" : NewBodyOperationType.ADD, "depth" : 4 * mm});
        }
        {
            var Q0;
            {var subQ0=sQuery(id+"F34.wireOp",EDGE,"E53.bottom");var subQ1=sQuery(id+"F36.wireOp",EDGE,"E55.left");Q0=makeQuery(id+"F45.opBoolean","SPLIT",FACE,{"disambiguationData":[TD([makeQuery(id+"F37.opExtrude","SWEPT_FACE",FACE,{"disambiguationData":[OSD([subQ1])]})])],"derivedFrom":makeQuery(id+"F35.opExtrude","SWEPT_FACE",FACE,{"disambiguationData":[OSD([subQ0])]})});}
            var sketch = newSketch(context, id + "F52", { "sketchPlane" : qUnion([Q0])});
            skLineSegment(sketch, "E77.rect.bottom", {"start": v(-9.94, -972.45) * mm, "end": v(-11.26, -972.45) * mm});
            skLineSegment(sketch, "E77.rect.top", {"start": v(-9.94, -975.96) * mm, "end": v(-11.26, -975.96) * mm});
            skLineSegment(sketch, "E77.rect.left", {"start": v(-9.94, -972.45) * mm, "end": v(-9.94, -975.96) * mm});
            skLineSegment(sketch, "E77.rect.right", {"start": v(-11.26, -972.45) * mm, "end": v(-11.26, -975.96) * mm});
            skPoint(sketch, "E77.rect.middle", {"position": v(-10.6, -974.2) * mm});
            skSolve(sketch);
        }
        {
            var Q0;
            Q0=qSketchRegion(id+"F52",true);
            extrude(context, id + "F53", {"entities" : qUnion([Q0]), "operationType" : NewBodyOperationType.REMOVE, "oppositeDirection" : true, "depth" : 5 * mm});
        }
        {
            var Q0;
            Q0=makeQuery(id+"F39.opExtrude","CAP_FACE",FACE,{"disambiguationData":[OSD([sQuery(id+"F38.wireOp",EDGE,"E57")])],"isStart":false});
            var sketch = newSketch(context, id + "F54", { "sketchPlane" : qUnion([Q0])});
            skCircle(sketch, "E78", {"center": v(-974.2, -289.6) * mm, "radius": 19.5 * mm});
            skSolve(sketch);
        }
        {
            var Q0;
            Q0=qSketchRegion(id+"F54",true);
            extrude(context, id + "F55", {"entities" : qUnion([Q0]), "depth" : 1 * mm});
        }
        {
            var Q0;
            Q0=makeQuery(id+"F55.opExtrude","CAP_FACE",FACE,{"disambiguationData":[OSD([sQuery(id+"F54.wireOp",EDGE,"E78")])],"isStart":false});
            var sketch = newSketch(context, id + "F56", { "sketchPlane" : qUnion([Q0])});
            skCircle(sketch, "E79", {"center": v(-974.2, -289.6) * mm, "radius": 15 * mm});
            skCircle(sketch, "E80", {"center": v(-974.2, -289.6) * mm, "radius": 15.58 * mm});
            skSolve(sketch);
        }
        {
            var Q0;
            Q0=qSketchRegion(id+"F56",true);
            extrude(context, id + "F57", {"entities" : qUnion([Q0]), "operationType" : NewBodyOperationType.ADD, "depth" : 6 * mm});
        }
        {
            var Q0;
            Q0=makeQuery(id+"F57.boolean.opBoolean","SPLIT",FACE,{"disambiguationData":[TD([makeQuery(id+"F57.opExtrude","SWEPT_FACE",FACE,{"disambiguationData":[OSD([sQuery(id+"F56.wireOp",EDGE,"E79")])]})])],"derivedFrom":makeQuery(id+"F55.opExtrude","CAP_FACE",FACE,{"disambiguationData":[OSD([sQuery(id+"F54.wireOp",EDGE,"E78")])],"isStart":false})});
            var sketch = newSketch(context, id + "F58", { "sketchPlane" : qUnion([Q0])});
            skCircle(sketch, "E81", {"center": v(-974.2, -289.6) * mm, "radius": 4.5 * mm});
            skSolve(sketch);
        }
        {
            var Q0;
            Q0=qSketchRegion(id+"F58",true);
            extrude(context, id + "F59", {"entities" : qUnion([Q0]), "operationType" : NewBodyOperationType.REMOVE, "oppositeDirection" : true, "depth" : 2 * mm});
        }
        {
            var Q0;
            {var subQ0=sQuery(id+"F54.wireOp",EDGE,"E78");Q0=makeQuery(id+"F57.boolean.opBoolean","SPLIT",FACE,{"disambiguationData":[TD([makeQuery(id+"F55.opExtrude","SWEPT_FACE",FACE,{"disambiguationData":[OSD([subQ0])]})])],"derivedFrom":makeQuery(id+"F55.opExtrude","CAP_FACE",FACE,{"disambiguationData":[OSD([subQ0])],"isStart":false})});}
            var sketch = newSketch(context, id + "F60", { "sketchPlane" : qUnion([Q0])});
            skLineSegment(sketch, "E82", {"start": v(-958.66, -288.7) * mm, "end": v(-958.05, -288.98) * mm});
            skLineSegment(sketch, "E83", {"start": v(-958.05, -288.98) * mm, "end": v(-958.05, -289.58) * mm});
            skLineSegment(sketch, "E84", {"start": v(-958.05, -289.58) * mm, "end": v(-958.63, -289.87) * mm});
            skLineSegment(sketch, "E85", {"start": v(-958.63, -289.87) * mm, "end": v(-958.66, -288.7) * mm});
            skSolve(sketch);
        }
        {
            var Q0;
            Q0=qSketchRegion(id+"F60",true);
            extrude(context, id + "F61", {"entities" : qUnion([Q0]), "depth" : 6 * mm});
        }
        {
            var Q0;
            Q0=makeQuery(id+"F61.opExtrude","SWEPT_BODY",BODY,{"disambiguationData":[OSD([sQuery(id+"F60.wireOp",EDGE,"E82"),sQuery(id+"F60.wireOp",EDGE,"E83"),sQuery(id+"F60.wireOp",EDGE,"E84"),sQuery(id+"F60.wireOp",EDGE,"E85")])]});
            var Q1;
            Q1=makeQuery(id+"F57.opExtrude","CAP_EDGE",EDGE,{"disambiguationData":[OSD([sQuery(id+"F56.wireOp",EDGE,"E80")])],"isStart":false});
            circularPattern(context, id + "F62", {"entities" : qUnion([Q0]), "axis" : qUnion([Q1]), "angle" : 5 * degree, "instanceCount" : round(75), "computeTransformsWithoutBuiltin" : true});
        }
        {
            var Q0;
            Q0=makeQuery(id+"F57.boolean.opBoolean","SPLIT",FACE,{"disambiguationData":[TD([makeQuery(id+"F57.opExtrude","SWEPT_FACE",FACE,{"disambiguationData":[OSD([sQuery(id+"F56.wireOp",EDGE,"E79")])]})])],"derivedFrom":makeQuery(id+"F55.opExtrude","CAP_FACE",FACE,{"disambiguationData":[OSD([sQuery(id+"F54.wireOp",EDGE,"E78")])],"isStart":false})});
            var sketch = newSketch(context, id + "F63", { "sketchPlane" : qUnion([Q0])});
            skCircle(sketch, "E86", {"center": v(-974.2, -289.6) * mm, "radius": 5 * mm});
            skCircle(sketch, "E87", {"center": v(-974.2, -289.6) * mm, "radius": 4.5 * mm});
            skSolve(sketch);
        }
        {
            var Q0;
            Q0=qSketchRegion(id+"F63",true);
            extrude(context, id + "F64", {"entities" : qUnion([Q0]), "operationType" : NewBodyOperationType.ADD, "depth" : 6 * mm});
        }
        {
            var Q0;
            Q0=makeQuery(id+"F9.opExtrude","SWEPT_FACE",FACE,{"disambiguationData":[OSD([sQuery(id+"F8.wireOp",EDGE,"E11.right")])]});
            var sketch = newSketch(context, id + "F65", { "sketchPlane" : qUnion([Q0])});
            skCircle(sketch, "E88", {"center": v(-993, -674.5) * mm, "radius": 1.5 * mm});
            skSolve(sketch);
        }
        {
            var Q0;
            Q0=qSketchRegion(id+"F65",true);
            extrude(context, id + "F66", {"entities" : qUnion([Q0]), "operationType" : NewBodyOperationType.REMOVE, "oppositeDirection" : true, "depth" : 20 * mm});
        }
        {
            var Q0;
            Q0=makeQuery(id+"F9.opExtrude","SWEPT_FACE",FACE,{"disambiguationData":[OSD([sQuery(id+"F8.wireOp",EDGE,"E11.right")])]});
            var sketch = newSketch(context, id + "F67", { "sketchPlane" : qUnion([Q0])});
            skCircle(sketch, "E89", {"center": v(-978.43, -501.64) * mm, "radius": 1.5 * mm});
            skSolve(sketch);
        }
        {
            var Q0;
            Q0=qSketchRegion(id+"F67",true);
            extrude(context, id + "F68", {"entities" : qUnion([Q0]), "depth" : 15 * mm, "symmetric" : true});
        }
        {
            var Q0;
            Q0=makeQuery(id+"F68.opExtrude","CAP_FACE",FACE,{"disambiguationData":[OSD([sQuery(id+"F67.wireOp",EDGE,"E89")])],"isStart":true});
            var sketch = newSketch(context, id + "F69", { "sketchPlane" : qUnion([Q0])});
            skCircle(sketch, "E90", {"center": v(978.43, -501.64) * mm, "radius": 2.5 * mm});
            skSolve(sketch);
        }
        {
            var Q0;
            Q0=qSketchRegion(id+"F69",true);
            extrude(context, id + "F70", {"entities" : qUnion([Q0]), "operationType" : NewBodyOperationType.ADD, "depth" : 2 * mm});
        }
        {
            var Q0;
            Q0=makeQuery(id+"F70.opExtrude","CAP_FACE",FACE,{"disambiguationData":[OSD([sQuery(id+"F69.wireOp",EDGE,"E90")])],"isStart":false});
            var sketch = newSketch(context, id + "F71", { "sketchPlane" : qUnion([Q0])});
            skLineSegment(sketch, "E91.rect.bottom", {"start": v(980.93, -501.84) * mm, "end": v(978.63, -501.84) * mm});
            skLineSegment(sketch, "E91.rect.top", {"start": v(980.93, -501.44) * mm, "end": v(978.63, -501.44) * mm});
            skLineSegment(sketch, "E91.rect.left", {"start": v(980.93, -501.84) * mm, "end": v(980.93, -501.44) * mm});
            skLineSegment(sketch, "E91.rect.right", {"start": v(975.93, -501.84) * mm, "end": v(975.93, -501.44) * mm});
            skPoint(sketch, "E91.rect.middle", {"position": v(978.43, -501.64) * mm});
            skLineSegment(sketch, "E92.rect.bottom", {"start": v(978.63, -504.14) * mm, "end": v(978.23, -504.14) * mm});
            skLineSegment(sketch, "E92.rect.top", {"start": v(978.63, -499.14) * mm, "end": v(978.23, -499.14) * mm});
            skLineSegment(sketch, "E92.rect.left", {"start": v(978.63, -504.14) * mm, "end": v(978.63, -501.84) * mm});
            skLineSegment(sketch, "E92.rect.right", {"start": v(978.23, -504.14) * mm, "end": v(978.23, -501.84) * mm});
            skLineSegment(sketch, "E93.trimOffspring", {"start": v(978.63, -501.44) * mm, "end": v(978.63, -499.14) * mm});
            skLineSegment(sketch, "E94.trimOffspring", {"start": v(978.23, -501.84) * mm, "end": v(975.93, -501.84) * mm});
            skLineSegment(sketch, "E95.trimOffspring", {"start": v(978.23, -501.44) * mm, "end": v(975.93, -501.44) * mm});
            skLineSegment(sketch, "E96.trimOffspring", {"start": v(978.23, -501.44) * mm, "end": v(978.23, -499.14) * mm});
            skSolve(sketch);
        }
        {
            var Q0;
            Q0=qSketchRegion(id+"F71",true);
            extrude(context, id + "F72", {"entities" : qUnion([Q0]), "operationType" : NewBodyOperationType.REMOVE, "oppositeDirection" : true, "depth" : 1 * mm});
        }
        {
            var Q0;
            {var subQ0=sQuery(id+"F69.wireOp",EDGE,"E90");Q0=makeQuery(id+"F72.boolean.opBoolean","SPLIT",EDGE,{"disambiguationData":[TD([makeQuery(id+"F72.opExtrude","SWEPT_FACE",FACE,{"disambiguationData":[OSD([sQuery(id+"F71.wireOp",EDGE,"E91.rect.top")])]})])],"derivedFrom":makeQuery(id+"F70.opExtrude","CAP_EDGE",EDGE,{"disambiguationData":[OSD([subQ0])],"isStart":false})});}
            var Q1;
            {var subQ0=sQuery(id+"F69.wireOp",EDGE,"E90");Q1=makeQuery(id+"F72.boolean.opBoolean","SPLIT",EDGE,{"disambiguationData":[TD([makeQuery(id+"F72.opExtrude","SWEPT_FACE",FACE,{"disambiguationData":[OSD([sQuery(id+"F71.wireOp",EDGE,"E95.trimOffspring")])]})])],"derivedFrom":makeQuery(id+"F70.opExtrude","CAP_EDGE",EDGE,{"disambiguationData":[OSD([subQ0])],"isStart":false})});}
            var Q2;
            {var subQ0=sQuery(id+"F69.wireOp",EDGE,"E90");Q2=makeQuery(id+"F72.boolean.opBoolean","SPLIT",EDGE,{"disambiguationData":[TD([makeQuery(id+"F72.opExtrude","SWEPT_FACE",FACE,{"disambiguationData":[OSD([sQuery(id+"F71.wireOp",EDGE,"E92.rect.right")])]})])],"derivedFrom":makeQuery(id+"F70.opExtrude","CAP_EDGE",EDGE,{"disambiguationData":[OSD([subQ0])],"isStart":false})});}
            var Q3;
            {var subQ0=sQuery(id+"F69.wireOp",EDGE,"E90");Q3=makeQuery(id+"F72.boolean.opBoolean","SPLIT",EDGE,{"disambiguationData":[TD([makeQuery(id+"F72.opExtrude","SWEPT_FACE",FACE,{"disambiguationData":[OSD([sQuery(id+"F71.wireOp",EDGE,"E91.rect.bottom")])]})])],"derivedFrom":makeQuery(id+"F70.opExtrude","CAP_EDGE",EDGE,{"disambiguationData":[OSD([subQ0])],"isStart":false})});}
            fillet(context, id + "F73", {"entities" : qUnion([Q0, Q1, Q2, Q3]), "radius" : 1 * mm, "tangentPropagation" : true, "allowEdgeOverflow" : false});
        }
        {
            var Q0;
            Q0=makeQuery(id+"F1.opExtrude","SWEPT_FACE",FACE,{"disambiguationData":[OSD([sQuery(id+"F0.wireOp",EDGE,"E0.rect.top")])]});
            var sketch = newSketch(context, id + "F74", { "sketchPlane" : qUnion([Q0])});
            skCircle(sketch, "E97", {"center": v(26.34, 25.9) * mm, "radius": 5 * mm});
            skSolve(sketch);
        }
        {
            var Q0;
            Q0=qSketchRegion(id+"F74",true);
            extrude(context, id + "F75", {"entities" : qUnion([Q0]), "oppositeDirection" : true, "depth" : 520 * mm});
        }
        {
            var Q0;
            Q0=qSketchRegion(id+"F0",true);
            extrude(context, id + "F76", {"entities" : qUnion([Q0]), "oppositeDirection" : true, "depth" : 300 * mm});
        }
        {
            var Q0;
            Q0=makeQuery(id+"F76.opExtrude","SWEPT_FACE",FACE,{"disambiguationData":[OSD([sQuery(id+"F0.wireOp",EDGE,"E0.rect.bottom")])]});
            var sketch = newSketch(context, id + "F77", { "sketchPlane" : qUnion([Q0])});
            skCircle(sketch, "E98", {"center": v(0, 0) * mm, "radius": 5 * mm});
            skSolve(sketch);
        }
        {
            var Q0;
            Q0=qSketchRegion(id+"F77",true);
            extrude(context, id + "F78", {"entities" : qUnion([Q0]), "operationType" : NewBodyOperationType.REMOVE, "oppositeDirection" : true, "depth" : 25 * mm});
        }
        {
            var Q0;
            Q0=makeQuery(id+"F1.opExtrude","SWEPT_FACE",FACE,{"disambiguationData":[OSD([sQuery(id+"F0.wireOp",EDGE,"E0.rect.bottom")])]});
            var sketch = newSketch(context, id + "F79", { "sketchPlane" : qUnion([Q0])});
            skLineSegment(sketch, "E99.rect.bottom", {"start": v(74.17, -761.82) * mm, "end": v(84.17, -761.82) * mm});
            skLineSegment(sketch, "E99.rect.top", {"start": v(74.17, -751.82) * mm, "end": v(84.17, -751.82) * mm});
            skLineSegment(sketch, "E99.rect.left", {"start": v(74.17, -761.82) * mm, "end": v(74.17, -751.82) * mm});
            skLineSegment(sketch, "E99.rect.right", {"start": v(84.17, -761.82) * mm, "end": v(84.17, -751.82) * mm});
            skPoint(sketch, "E99.rect.middle", {"position": v(79.17, -756.82) * mm});
            skLineSegment(sketch, "E100.rect.bottom", {"start": v(74.67, -761.32) * mm, "end": v(83.67, -761.32) * mm});
            skLineSegment(sketch, "E100.rect.top", {"start": v(74.67, -752.32) * mm, "end": v(83.67, -752.32) * mm});
            skLineSegment(sketch, "E100.rect.left", {"start": v(74.67, -761.32) * mm, "end": v(74.67, -752.32) * mm});
            skLineSegment(sketch, "E100.rect.right", {"start": v(83.67, -761.32) * mm, "end": v(83.67, -752.32) * mm});
            skSolve(sketch);
        }
        {
            var Q0;
            Q0=qSketchRegion(id+"F79",true);
            extrude(context, id + "F80", {"entities" : qUnion([Q0]), "oppositeDirection" : true, "depth" : 420 * mm});
        }
        {
            var Q0;
            Q0=makeQuery(id+"F80.opExtrude","SWEPT_FACE",FACE,{"disambiguationData":[OSD([sQuery(id+"F79.wireOp",EDGE,"E99.rect.right")])]});
            var sketch = newSketch(context, id + "F81", { "sketchPlane" : qUnion([Q0])});
            skLineSegment(sketch, "E101", {"start": v(-751.82, 7.5) * mm, "end": v(-761.82, -2.5) * mm});
            skLineSegment(sketch, "E102", {"start": v(-761.82, -2.5) * mm, "end": v(-761.82, 7.5) * mm});
            skLineSegment(sketch, "E103", {"start": v(-761.82, 7.5) * mm, "end": v(-751.82, 7.5) * mm});
            skSolve(sketch);
        }
        {
            var Q0;
            Q0=qSketchRegion(id+"F81",true);
            extrude(context, id + "F82", {"entities" : qUnion([Q0]), "operationType" : NewBodyOperationType.REMOVE, "oppositeDirection" : true, "depth" : 10 * mm});
        }
        {
            var Q0;
            Q0=makeQuery(id+"F80.opExtrude","SWEPT_FACE",FACE,{"disambiguationData":[OSD([sQuery(id+"F79.wireOp",EDGE,"E99.rect.right")])]});
            var sketch = newSketch(context, id + "F83", { "sketchPlane" : qUnion([Q0])});
            skLineSegment(sketch, "E104", {"start": v(-751.82, -412.5) * mm, "end": v(-761.82, -402.5) * mm});
            skLineSegment(sketch, "E105", {"start": v(-761.82, -402.5) * mm, "end": v(-761.82, -412.5) * mm});
            skLineSegment(sketch, "E106", {"start": v(-761.82, -412.5) * mm, "end": v(-751.82, -412.5) * mm});
            skSolve(sketch);
        }
        {
            var Q0;
            Q0=qSketchRegion(id+"F83",true);
            extrude(context, id + "F84", {"entities" : qUnion([Q0]), "operationType" : NewBodyOperationType.REMOVE, "oppositeDirection" : true, "depth" : 10 * mm});
        }
    });
